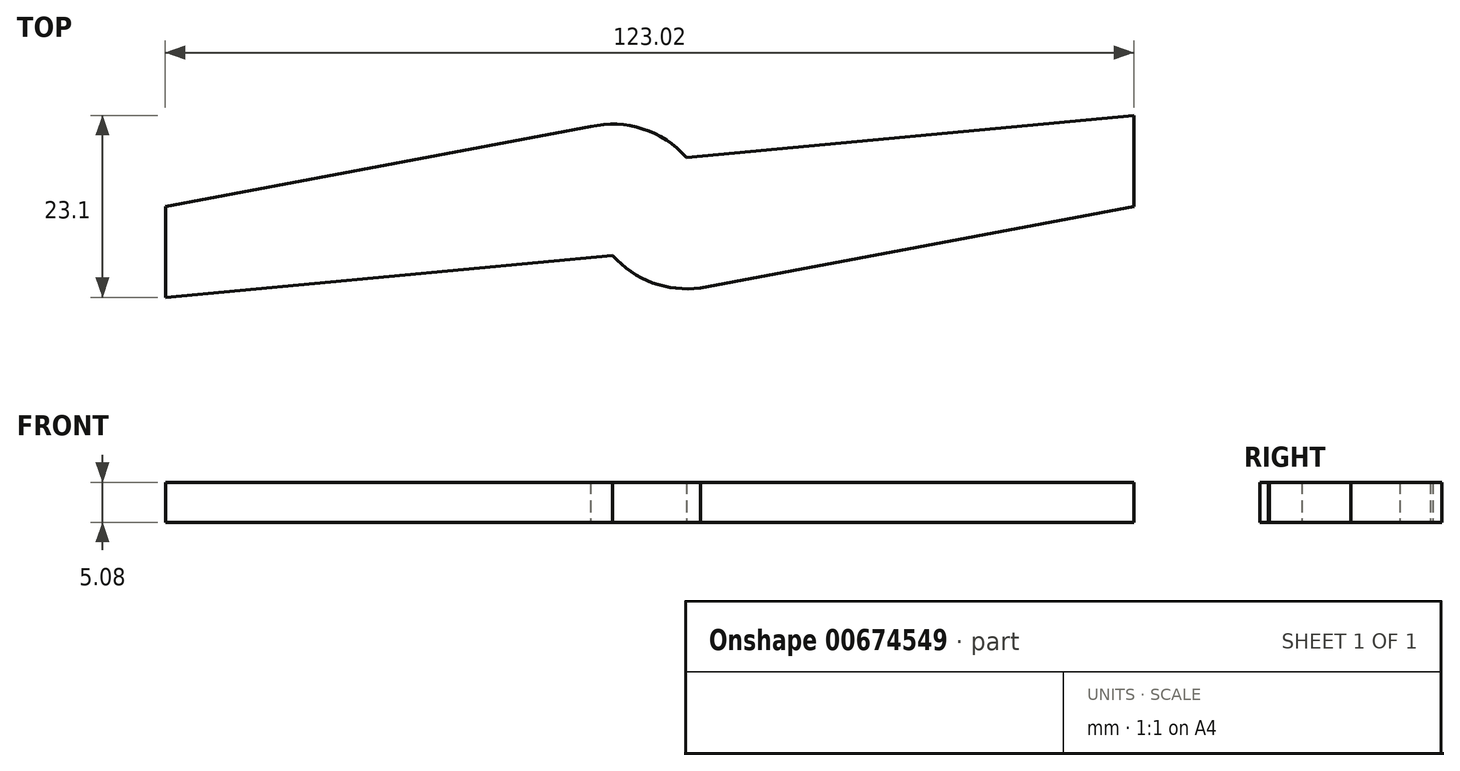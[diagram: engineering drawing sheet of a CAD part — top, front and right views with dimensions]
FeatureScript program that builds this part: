
annotation { "Feature Type Name" : "Feature", "Feature Type Description" : "" }
export const myFeature = defineFeature(function(context is Context, id is Id, definition is map)
    precondition{}
    {
        {
            var Q0;
            Q0=qCreatedBy(makeId("Top.planeOp"),FACE);
            var sketch = newSketch(context, id + "F0", { "sketchPlane" : qUnion([Q0])});
            skLineSegment(sketch, "E0.left", {"start": v(-61.5, 0) * mm, "end": v(-61.5, -11.55) * mm});
            skLineSegment(sketch, "E0.right", {"start": v(61.5, 11.55) * mm, "end": v(61.5, 0) * mm});
            skPoint(sketch, "E0.middle", {"position": v(0, 0) * mm});
            skLineSegment(sketch, "E1", {"start": v(-61.5, 0) * mm, "end": v(-6.47, 10.33) * mm});
            skLineSegment(sketch, "E2", {"start": v(0, -11.55) * mm, "end": v(61.5, 0) * mm});
            skArc(sketch, "E3", {"start": v(-4.68, -6.23) * mm, "mid": v(0.86, -9.87) * mm, "end": v(7.49, -10.14) * mm});
            skArc(sketch, "E4", {"start": v(4.67, 6.23) * mm, "mid": v(-0.87, 9.86) * mm, "end": v(-7.49, 10.14) * mm});
            skPoint(sketch, "E5.orphan", {"position": v(61.5, -11.55) * mm});
            skPoint(sketch, "E6.orphan", {"position": v(-61.5, 11.55) * mm});
            skPoint(sketch, "E0.bottom.start.orphan", {"position": v(0, 11.55) * mm});
            skLineSegment(sketch, "E7", {"start": v(-61.5, -11.55) * mm, "end": v(-4.68, -6.23) * mm});
            skLineSegment(sketch, "E8", {"start": v(4.67, 6.23) * mm, "end": v(61.5, 11.55) * mm});
            skPoint(sketch, "E9.orphan", {"position": v(7.62, 0) * mm});
            skPoint(sketch, "E10.orphan", {"position": v(-7.62, 0) * mm});
            skSolve(sketch);
        }
        {
            var Q0;
            {var subQ0=sQuery(id+"F0.wireOp",EDGE,"E4");var subQ1=sQuery(id+"F0.wireOp",EDGE,"E1");var subQ2=makeQuery(id+"F0.imprint","INTERSECT",VERTEX,{"disambiguationData":[OD(0.0)],"derivedFrom":[subQ1,subQ0]});Q0=makeQuery(id+"F0.imprint","IMPRINT",FACE,{"disambiguationData":[TD([[makeQuery(id+"F0.imprint","IMPRINT",EDGE,{"disambiguationData":[TD([[subQ2,1.0]])],"derivedFrom":subQ1}),1.0]])]});}
            var Q1;
            {var subQ0=sQuery(id+"F0.wireOp",EDGE,"E3");var subQ1=sQuery(id+"F0.wireOp",EDGE,"E2");var subQ2=makeQuery(id+"F0.imprint","INTERSECT",VERTEX,{"disambiguationData":[OD(0.0)],"derivedFrom":[subQ1,subQ0]});Q1=makeQuery(id+"F0.imprint","IMPRINT",FACE,{"disambiguationData":[TD([[makeQuery(id+"F0.imprint","IMPRINT",EDGE,{"disambiguationData":[TD([[subQ2,1.0]])],"derivedFrom":subQ1}),-1.0]])]});}
            var Q2;
            {var subQ4=sQuery(id+"F0.wireOp",EDGE,"E0.left");Q2=makeQuery(id+"F0.imprint","IMPRINT",FACE,{"disambiguationData":[TD([[makeQuery(id+"F0.imprint","IMPRINT",EDGE,{"derivedFrom":subQ4}),1.0]])]});}
            extrude(context, id + "F1", {"entities" : qUnion([Q0, Q1, Q2]), "depth" : 5.08 * mm, "offsetDistance" : 25.4 * mm});
        }
    });
